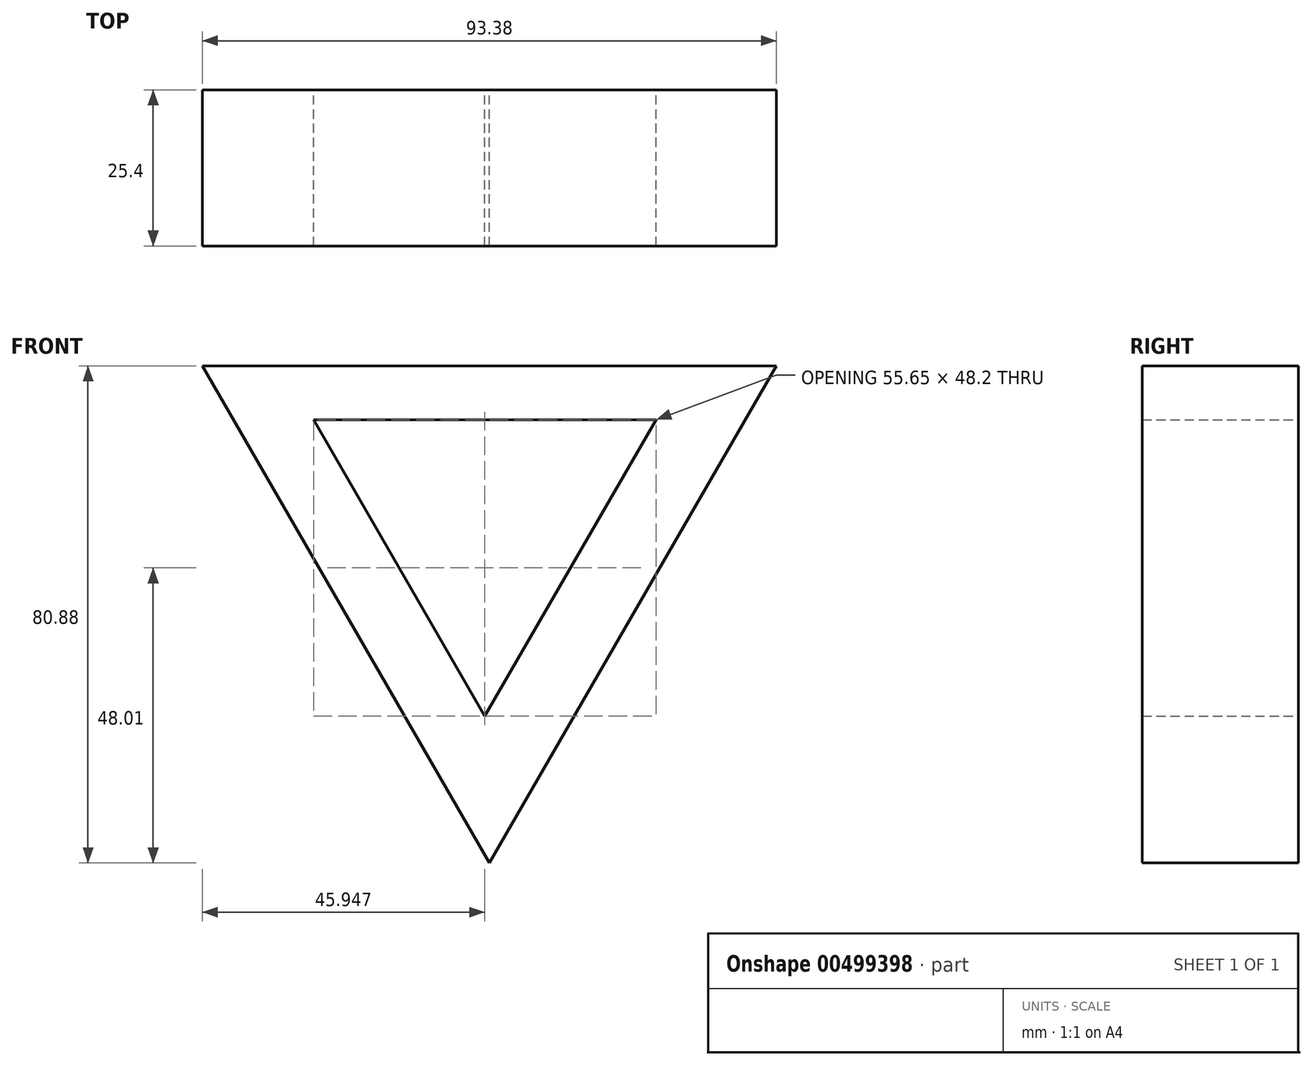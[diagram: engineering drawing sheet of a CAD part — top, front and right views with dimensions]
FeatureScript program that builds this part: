
annotation { "Feature Type Name" : "Feature", "Feature Type Description" : "" }
export const myFeature = defineFeature(function(context is Context, id is Id, definition is map)
    precondition{}
    {
        {
            var Q0;
            Q0=qCreatedBy(makeId("Front.planeOp"),FACE);
            var sketch = newSketch(context, id + "F0", { "sketchPlane" : qUnion([Q0])});
            skLineSegment(sketch, "E0", {"start": v(0, 0) * mm, "end": v(-46.7, 80.88) * mm});
            skLineSegment(sketch, "E1", {"start": v(-46.7, 80.88) * mm, "end": v(46.7, 80.88) * mm});
            skLineSegment(sketch, "E2", {"start": v(46.7, 80.88) * mm, "end": v(0, 0) * mm});
            skLineSegment(sketch, "E3", {"start": v(-28.57, 72.1) * mm, "end": v(-0.74, 23.91) * mm});
            skLineSegment(sketch, "E4", {"start": v(-0.74, 23.91) * mm, "end": v(27.08, 72.1) * mm});
            skLineSegment(sketch, "E5", {"start": v(27.08, 72.1) * mm, "end": v(-28.57, 72.1) * mm});
            skSolve(sketch);
        }
        {
            var Q0;
            Q0 = qSketchRegion(id + "F0", true);
            extrude(context, id + "F1", {"entities" : qUnion([Q0]), "depth" : 25.4 * mm});
        }
    });
